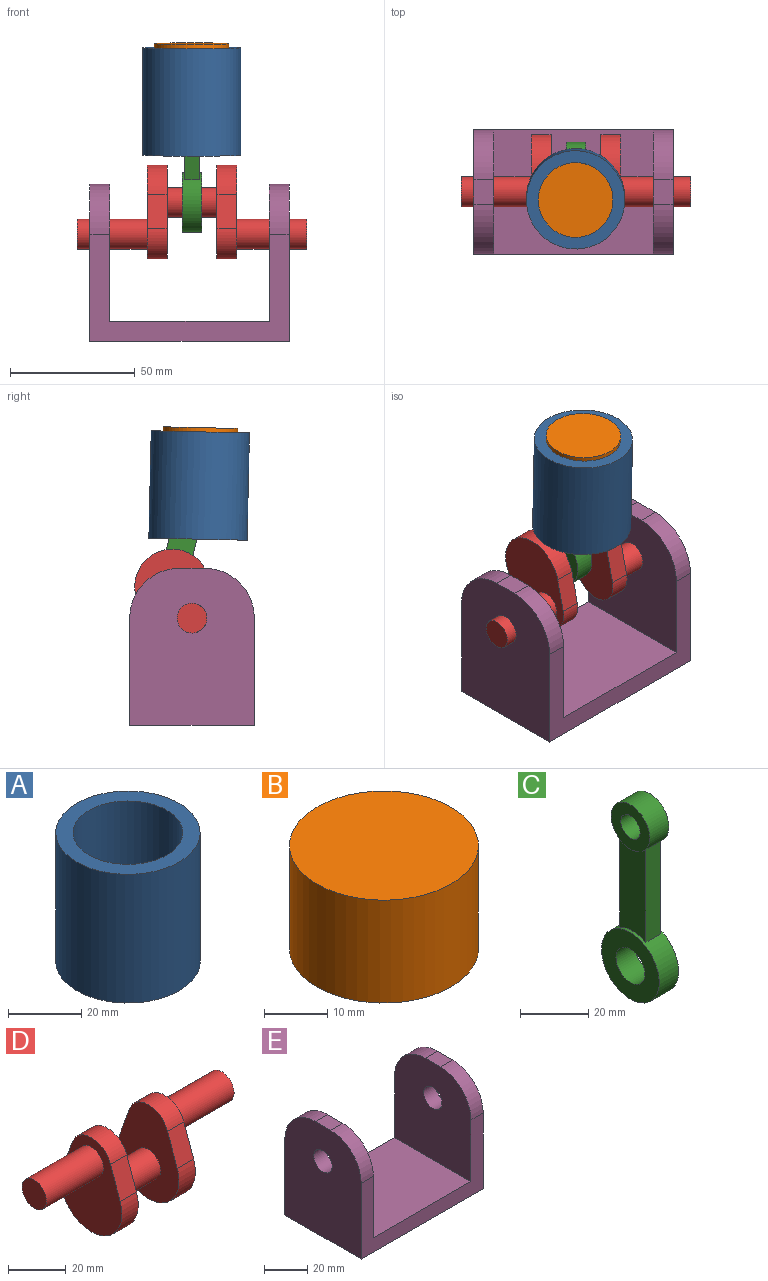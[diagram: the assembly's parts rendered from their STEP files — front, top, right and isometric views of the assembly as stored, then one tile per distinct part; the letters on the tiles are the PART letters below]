
ASSEMBLY  parts=5 mates=4
PART A: 4 faces, bbox 39.5x39.5x43.1 mm
  f0: plane 39.46x39.46mm, normal (0,0,-1), area 516.3mm2, adj f1,f3
  f1: cylinder r=19.73mm len=43.07mm, axis (0,0,-1), area 5339.7mm2, adj f0,f2
  f2: plane 39.46x39.46mm, normal (0,0,1), area 516.3mm2, adj f1,f3
  f3: cylinder r=15mm len=43.07mm, axis (0,0,-1), area 4059.1mm2, adj f0,f2
PART B: 6 faces, bbox 30x30x20 mm
  f0: cylinder r=12mm len=24mm, axis (0,0,-1), area 1144.3mm2, adj f1,f2,f5
  f1: plane 24x24mm, normal (0,0,-1), area 452.4mm2, adj f0
  f2: plane 30x30mm, normal (0,0,-1), area 254.5mm2, adj f0,f3
  f3: cylinder r=15mm len=30mm, axis (0,0,-1), area 1885mm2, adj f2,f4
  f4: plane 30x30mm, normal (0,0,1), area 706.9mm2, adj f3
  f5: cylinder r=4mm len=24mm, axis (-1,0,0), area 586.1mm2, adj f0
PART C: 12 faces, bbox 8x24x70 mm
  f0: cylinder r=6mm len=12mm, axis (-1,0,0), area 301.6mm2, adj f2,f3
  f1: cylinder r=12mm len=24mm, axis (-1,0,0), area 535.2mm2, adj f2,f3,f4,f5,f6,f7
  f2: plane 24x24mm, normal (1,0,0), area 339.3mm2, adj f0,f1
  f3: plane 24x24mm, normal (-1,0,0), area 339.3mm2, adj f0,f1
  f4: plane 33.47x6mm, normal (0,1,0), area 200.8mm2, adj f1,f6,f7,f8
  f5: plane 33.47x6mm, normal (0,-1,0), area 200.8mm2, adj f1,f6,f7,f8
  f6: plane 33.47x10.92mm, normal (1,0,0), area 339.7mm2, adj f1,f4,f5,f8
  f7: plane 33.47x10.92mm, normal (-1,0,0), area 339.7mm2, adj f1,f4,f5,f8
  f8: cylinder r=8mm len=16mm, axis (-1,0,0), area 330mm2, adj f4,f5,f6,f7,f10,f11
  f9: cylinder r=4mm len=8mm, axis (-1,0,0), area 201.1mm2, adj f10,f11
  f10: plane 16x16mm, normal (1,0,0), area 150.8mm2, adj f8,f9
  f11: plane 16x16mm, normal (-1,0,0), area 150.8mm2, adj f8,f9
PART D: 17 faces, bbox 92x30x40 mm
  f0: plane 13.33x8mm, normal (0,0.94,0.33), area 113.1mm2, adj f1,f3,f4,f5
  f1: cylinder r=10mm len=18.86mm, axis (-1,0,0), area 197mm2, adj f0,f2,f4,f5
  f2: plane 13.33x8mm, normal (0,-0.94,0.33), area 113.1mm2, adj f1,f3,f4,f5
  f3: cylinder r=15mm len=30mm, axis (-1,0,0), area 458.6mm2, adj f0,f2,f4,f5
  f4: plane 40x30mm, normal (1,0,0), area 793.4mm2, adj f0,f1,f2,f3,f7
  f5: plane 40x30mm, normal (-1,0,0), area 793.4mm2, adj f0,f1,f2,f3,f6
  f6: cylinder r=6mm len=20mm, axis (1,0,0), area 754mm2, adj f5,f13
  f7: cylinder r=6mm len=28mm, axis (-1,0,0), area 1055.6mm2, adj f4,f15
  f8: plane 13.33x8mm, normal (0,0.94,0.33), area 113.1mm2, adj f9,f11,f12,f13
  f9: cylinder r=10mm len=18.86mm, axis (1,0,0), area 197mm2, adj f8,f10,f12,f13
  f10: plane 13.33x8mm, normal (0,-0.94,0.33), area 113.1mm2, adj f9,f11,f12,f13
  f11: cylinder r=15mm len=30mm, axis (1,0,0), area 458.6mm2, adj f8,f10,f12,f13
  f12: plane 40x30mm, normal (-1,0,0), area 793.4mm2, adj f8,f9,f10,f11,f14
  f13: plane 40x30mm, normal (1,0,0), area 793.4mm2, adj f6,f8,f9,f10,f11
  f14: cylinder r=6mm len=28mm, axis (1,0,0), area 1055.6mm2, adj f12,f16
  f15: plane 12x12mm, normal (1,0,0), area 113.1mm2, adj f7
  f16: plane 12x12mm, normal (-1,0,0), area 113.1mm2, adj f14
PART E: 16 faces, bbox 80x50x63 mm
  f0: plane 64x50mm, normal (0,0,1), area 3200mm2, adj f1,f3,f6,f8
  f1: plane 80x43mm, normal (0,1,0), area 1200mm2, adj f0,f2,f4,f5,f6,f8,f12,f15
  f2: plane 63x50mm, normal (-1,0,0), area 2865.2mm2, adj f1,f3,f5,f9,f10,f12,f13
  f3: plane 80x43mm, normal (0,-1,0), area 1200mm2, adj f0,f2,f4,f5,f6,f8,f13,f14
  f4: plane 63x50mm, normal (1,0,0), area 2865.2mm2, adj f1,f3,f5,f7,f11,f14,f15
  f5: plane 80x50mm, normal (0,0,-1), area 4000mm2, adj f1,f2,f3,f4
  f6: plane 55x50mm, normal (-1,0,0), area 2465.2mm2, adj f0,f1,f3,f7,f11,f14,f15
  f7: plane 10x8mm, normal (0,0,1), area 80mm2, adj f4,f6,f14,f15
  f8: plane 55x50mm, normal (1,0,0), area 2465.2mm2, adj f0,f1,f3,f9,f10,f12,f13
  f9: plane 10x8mm, normal (0,0,1), area 80mm2, adj f2,f8,f12,f13
  f10: cylinder r=6mm len=12mm, axis (1,0,0), area 301.6mm2, adj f2,f8
  f11: cylinder r=6mm len=12mm, axis (1,0,0), area 301.6mm2, adj f4,f6
  f12: cylinder r=20mm len=20mm, axis (-1,0,0), area 251.3mm2, adj f1,f2,f8,f9
  f13: cylinder r=20mm len=20mm, axis (1,0,0), area 251.3mm2, adj f2,f3,f8,f9
  f14: cylinder r=20mm len=20mm, axis (1,0,0), area 251.3mm2, adj f3,f4,f6,f7
  f15: cylinder r=20mm len=20mm, axis (-1,0,0), area 251.3mm2, adj f1,f4,f6,f7
PLACE A rot(axis=(1,0,0),1.3deg) t=(0.85,-0.18,-33.27)mm fixed
PLACE B rot(axis=(1,0,0),1.3deg) t=(0.85,-2.94,91.46)mm
PLACE C rot(axis=(1,0,0),12.8deg) t=(1,7.99,47.69)mm
PLACE D rot(axis=(1,0,0),147.8deg) t=(11,7.99,47.69)mm
PLACE E at identity fixed
MATE revolute D.f1 <-> E.f10  axis (-1,0,0) through (-45,0,35)mm
MATE revolute C.f0 <-> D.f3  axis (1,0,0) through (5,7.99,47.69)mm
MATE revolute B.f5 <-> C.f8  axis (-1,0,0) through (13,-3.05,96.46)mm
MATE slider B.f0 <-> A.f1  axis (0,0.02,-1) through (0.85,-2.94,91.46)mm
